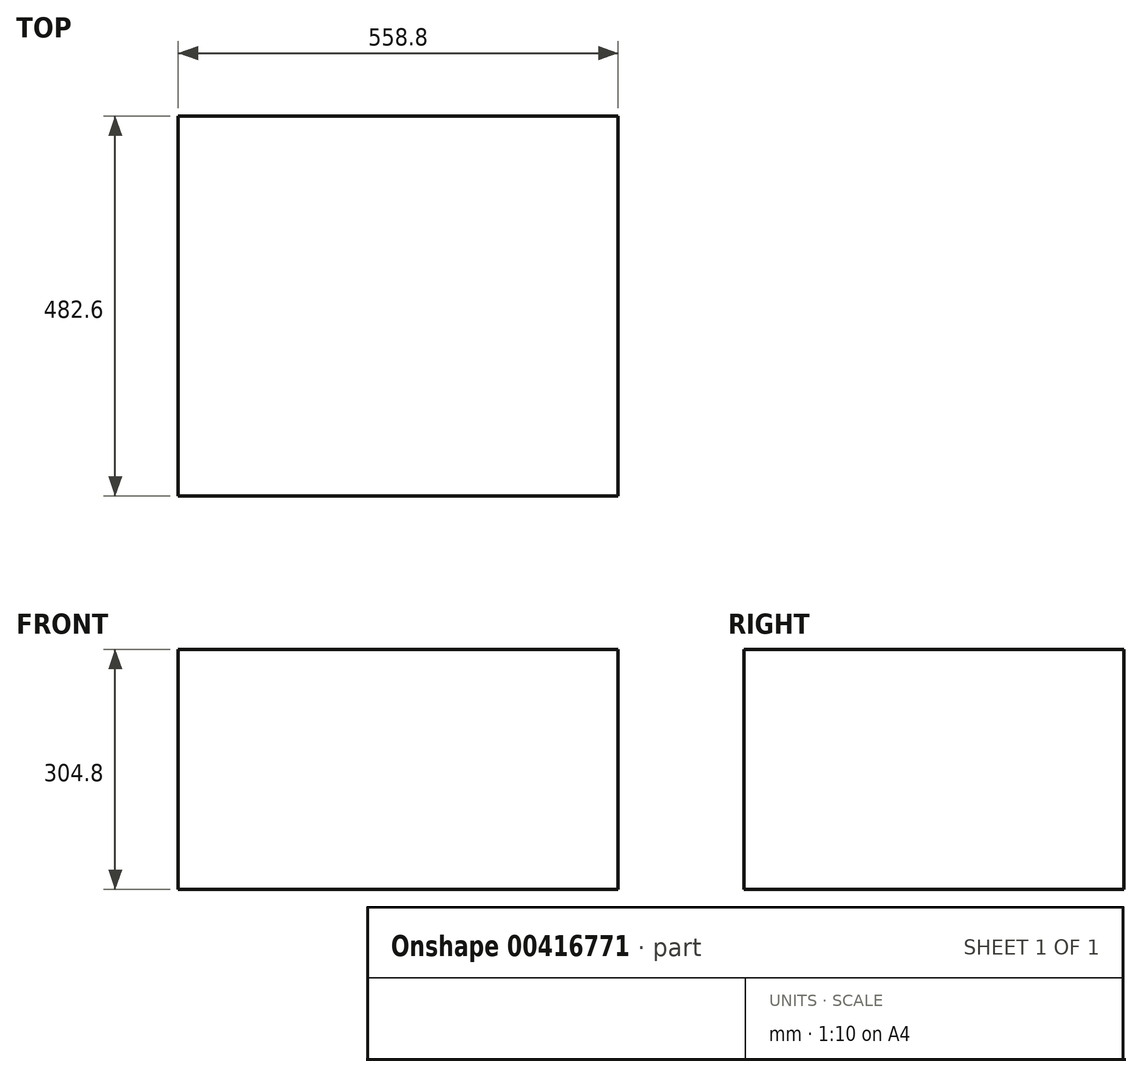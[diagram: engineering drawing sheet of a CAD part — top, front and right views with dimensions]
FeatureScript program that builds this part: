
annotation { "Feature Type Name" : "Feature", "Feature Type Description" : "" }
export const myFeature = defineFeature(function(context is Context, id is Id, definition is map)
    precondition{}
    {
        {
            var Q0;
            Q0=qCreatedBy(makeId("Front.planeOp"),FACE);
            var sketch = newSketch(context, id + "F0", { "sketchPlane" : qUnion([Q0])});
            skLineSegment(sketch, "E0.bottom", {"start": v(0, 0) * mm, "end": v(558.8, 0) * mm});
            skLineSegment(sketch, "E0.top", {"start": v(0, 304.8) * mm, "end": v(558.8, 304.8) * mm});
            skLineSegment(sketch, "E0.left", {"start": v(0, 0) * mm, "end": v(0, 304.8) * mm});
            skLineSegment(sketch, "E0.right", {"start": v(558.8, 0) * mm, "end": v(558.8, 304.8) * mm});
            skSolve(sketch);
        }
        {
            var Q0;
            Q0=makeQuery(id+"F0.imprint","IMPRINT",FACE,{"disambiguationData":[TD([[makeQuery(id+"F0.imprint","IMPRINT",EDGE,{"derivedFrom":sQuery(id+"F0.wireOp",EDGE,"E0.bottom")}),1.0]])]});
            extrude(context, id + "F1", {"entities" : qUnion([Q0]), "depth" : 482.6 * mm});
        }
    });
